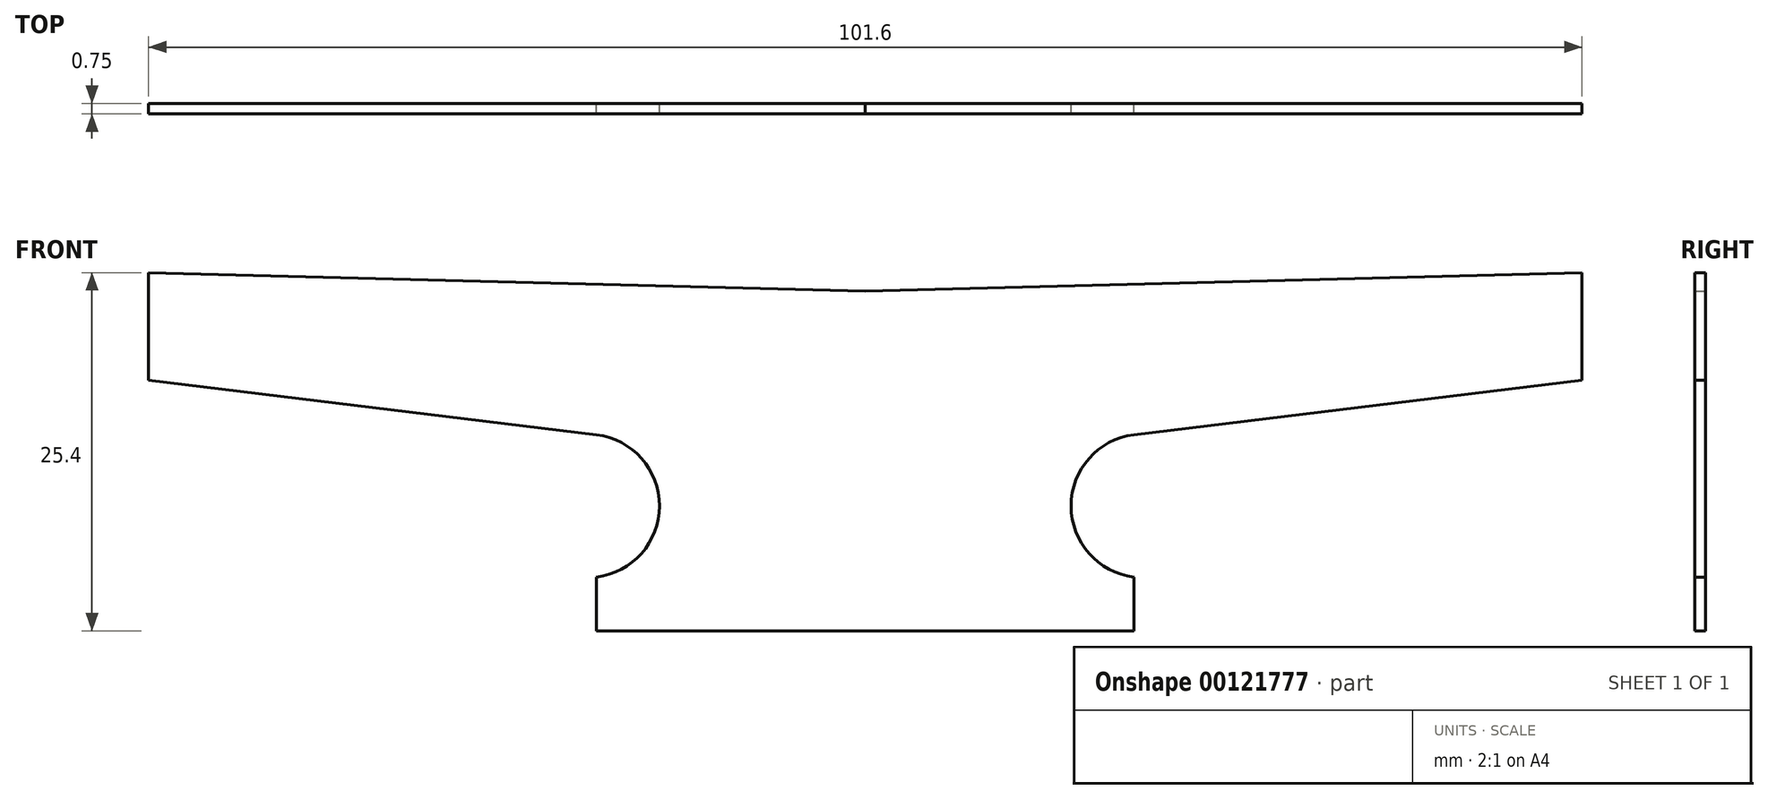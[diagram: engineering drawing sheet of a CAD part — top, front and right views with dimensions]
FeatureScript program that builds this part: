
annotation { "Feature Type Name" : "Feature", "Feature Type Description" : "" }
export const myFeature = defineFeature(function(context is Context, id is Id, definition is map)
    precondition{}
    {
        {
            assignVariable(context, id + "F0", {"name" : "Thickness", "anyValue" : .75});
        }
        {
            var Q0;
            Q0=qCreatedBy(makeId("Front.planeOp"),FACE);
            var sketch = newSketch(context, id + "F1", { "sketchPlane" : qUnion([Q0])});
            skLineSegment(sketch, "E0.bottom", {"start": v(-50.8, 25.4) * mm, "end": v(0, 24.07) * mm});
            skLineSegment(sketch, "E0.top", {"start": v(-19.05, 0) * mm, "end": v(0, 0) * mm});
            skLineSegment(sketch, "E0.left", {"start": v(-50.8, 25.4) * mm, "end": v(-50.8, 17.78) * mm});
            skLineSegment(sketch, "E1", {"start": v(-50.8, 17.78) * mm, "end": v(-19.05, 13.9) * mm});
            skArc(sketch, "E2", {"start": v(-19.05, 3.8) * mm, "mid": v(-14.59, 8.85) * mm, "end": v(-19.05, 13.9) * mm});
            skLineSegment(sketch, "E3", {"start": v(-19.05, 3.81) * mm, "end": v(-19.05, 0) * mm});
            skLineSegment(sketch, "E4.MirrorCS", {"start": v(19.05, 3.81) * mm, "end": v(19.05, 0) * mm});
            skLineSegment(sketch, "E5.MirrorCS", {"start": v(19.05, 0) * mm, "end": v(0, 0) * mm});
            skLineSegment(sketch, "E6.MirrorCS", {"start": v(50.8, 25.4) * mm, "end": v(50.8, 17.78) * mm});
            skLineSegment(sketch, "E7.MirrorCS", {"start": v(50.8, 17.78) * mm, "end": v(19.05, 13.9) * mm});
            skLineSegment(sketch, "E8.MirrorCS", {"start": v(50.8, 25.4) * mm, "end": v(0, 24.07) * mm});
            skArc(sketch, "E9.MirrorCS", {"start": v(19.05, 3.8) * mm, "mid": v(14.59, 8.85) * mm, "end": v(19.05, 13.9) * mm});
            skSolve(sketch);
        }
        {
            var Q0;
            Q0 = qSketchRegion(id + "F1", true);
            extrude(context, id + "F2", {"entities" : qUnion([Q0]), "depth" : (getVariable(context, 'Thickness')) * mm});
        }
    });
